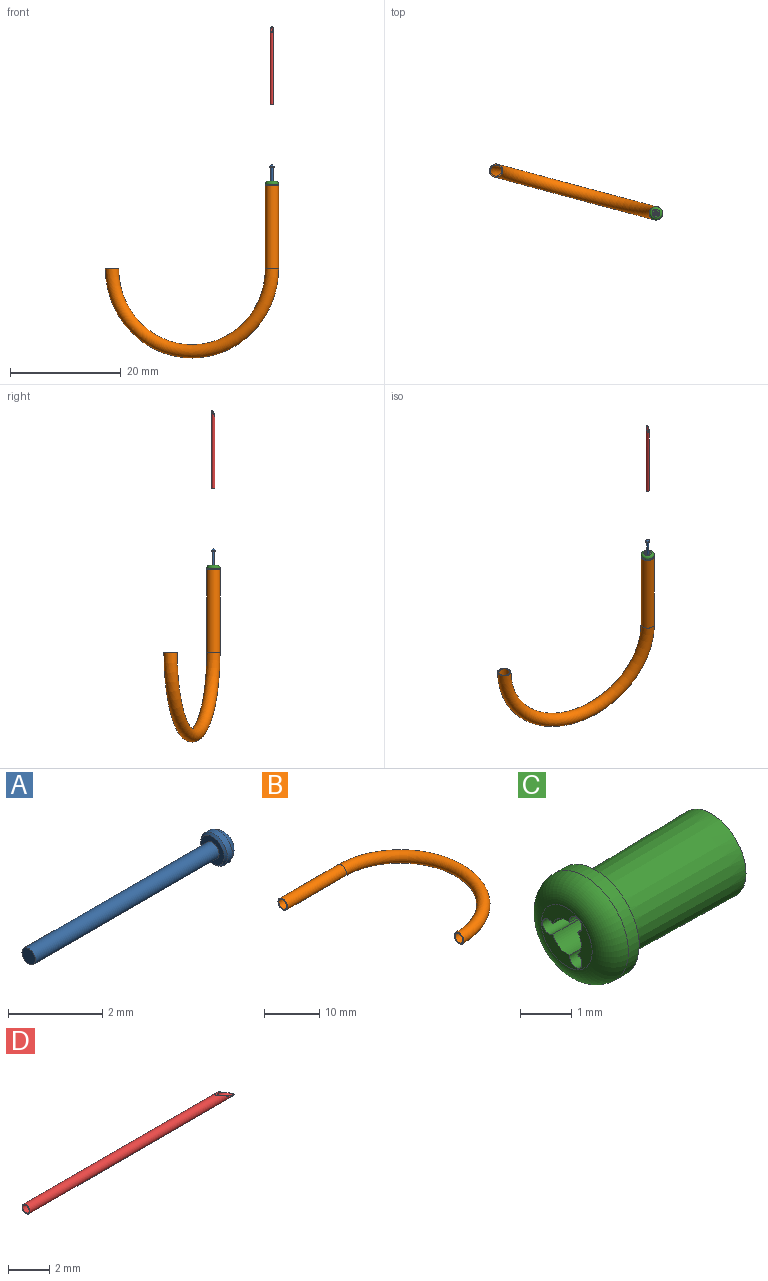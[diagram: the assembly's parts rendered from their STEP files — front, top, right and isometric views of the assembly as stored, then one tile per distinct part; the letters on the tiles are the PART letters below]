
ASSEMBLY  parts=4 mates=3
PART A: 6 faces, bbox 6x0.8x0.8 mm
  f0: cylinder r=0.2mm len=5.52mm, axis (1,0,0), area 6.9mm2, adj f1,f5
  f1: plane 0.4x0.4mm, normal (-1,0,0), area 0.1mm2, adj f0
  f2: sphere r=0.43mm, area 0.7mm2, adj f3
  f3: cylinder r=0.4mm len=0.8mm, axis (1,0,0), area 0.4mm2, adj f2,f4
  f4: cone r=0.35mm half-angle=45deg, axis (1,0,0), area 0.2mm2, adj f3,f5
  f5: plane 0.7x0.7mm, normal (-1,0,0), area 0.3mm2, adj f0,f4
PART B: 6 faces, bbox 32.5x35x2.4 mm
  f0: torus R=14.98mm, axis (0,0,1), area 295.7mm2, adj f1,f2
  f1: cylinder r=1mm len=15mm, axis (-1,0,0), area 94.2mm2, adj f0,f3
  f2: plane 2.4x2.4mm, normal (-1,0,0), area 1.4mm2, adj f0,f4
  f3: plane 2.4x2.4mm, normal (-1,0,0), area 1.4mm2, adj f1,f5
  f4: torus R=14.98mm, axis (0,0,1), area 354.8mm2, adj f2,f5
  f5: cylinder r=1.2mm len=15mm, axis (-1,0,0), area 113.1mm2, adj f3,f4
PART C: 15 faces, bbox 4x2.6x2.6 mm
  f0: cylinder r=0.4mm len=3.28mm, axis (-1,0,0), area 1.9mm2, adj f3,f7,f12,f14
  f1: cylinder r=0.4mm len=3.28mm, axis (-1,0,0), area 1.9mm2, adj f4,f7,f13,f14
  f2: cylinder r=0.4mm len=3.28mm, axis (-1,0,0), area 1.9mm2, adj f7,f8,f12,f13
  f3: torus R=0.9mm, axis (-1,0,0), area 0.3mm2, adj f0,f9,f12,f14
  f4: torus R=0.9mm, axis (-1,0,0), area 0.3mm2, adj f1,f9,f13,f14
  f5: cylinder r=1.2mm len=2.4mm, axis (-1,0,0), area 2.3mm2, adj f6,f11
  f6: torus R=0.7mm, axis (-1,0,0), area 5mm2, adj f5,f7
  f7: plane 1.41x1.41mm, normal (-1,0,0), area 0.8mm2, adj f0,f1,f2,f6,f12,f13,f14
  f8: torus R=0.9mm, axis (-1,0,0), area 0.3mm2, adj f2,f9,f12,f13
  f9: cone r=0.95mm half-angle=47.7deg, axis (1,0,0), area 2.5mm2, adj f3,f4,f8,f10,f12,f13,f14
  f10: cone r=0.95mm half-angle=0.9deg, axis (1,0,0), area 18.6mm2, adj f9,f11
  f11: plane 2.4x2.4mm, normal (1,0,0), area 2mm2, adj f5,f10
  f12: cylinder r=0.17mm len=3.75mm, axis (-1,0,0), area 2.9mm2, adj f0,f2,f3,f7,f8,f9
  f13: cylinder r=0.17mm len=3.75mm, axis (-1,0,0), area 2.9mm2, adj f1,f2,f4,f7,f8,f9
  f14: cylinder r=0.17mm len=3.75mm, axis (-1,0,0), area 2.9mm2, adj f0,f1,f3,f4,f7,f9
PART D: 6 faces, bbox 14.2x0.5x0.5 mm
  f0: cylinder r=0.22mm len=14.16mm, axis (-1,0,0), area 18.9mm2, adj f2,f3,f4,f5
  f1: cylinder r=0.27mm len=14.24mm, axis (-1,0,0), area 23.1mm2, adj f2,f3,f4,f5
  f2: plane 0.54x0.54mm, normal (-1,0,0), area 0.1mm2, adj f0,f1
  f3: plane 0.49x0.47mm, normal (0.31,0,0.95), area 0.1mm2, adj f0,f1,f4,f5
  f4: plane 0.82x0.4mm, normal (0.48,0.26,0.84), area 0.1mm2, adj f0,f1,f3,f5
  f5: plane 0.82x0.4mm, normal (0.48,-0.26,0.84), area 0.1mm2, adj f0,f1,f3,f4
PLACE A rot(axis=(-0.13,-0.98,-0.13),91deg) t=(-3.45,14.33,11.52)mm
PLACE B rot(axis=(0.62,0.48,-0.62),129deg) t=(-17.91,18.21,-5.12)mm
PLACE C rot(axis=(0.62,0.48,-0.62),129deg) t=(-3.45,14.33,9.61)mm
PLACE D rot(axis=(0.52,-0.68,0.52),111.8deg) t=(-3.45,14.33,25.96)mm
MATE slider D.f0 <-> C.f0  axis (0,0,-1) through (-3.45,14.33,31.7)mm
MATE slider A.f0 <-> C.f0  axis (0,0,1) through (-3.45,14.33,10.4)mm
MATE fastened C.f0 <-> B.f1  axis (0,0,-1) through (-3.45,14.33,9.88)mm
